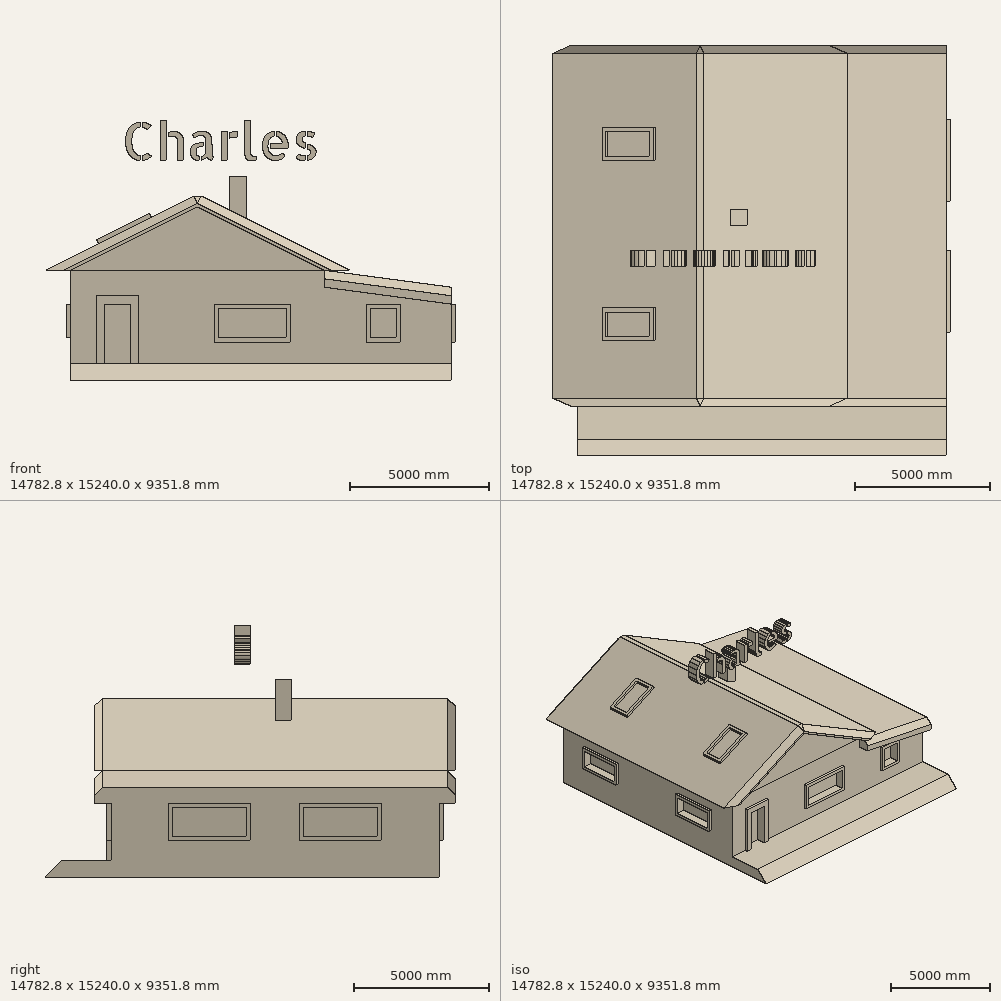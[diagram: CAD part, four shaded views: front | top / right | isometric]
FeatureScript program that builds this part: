
annotation { "Feature Type Name" : "Feature", "Feature Type Description" : "" }
export const myFeature = defineFeature(function(context is Context, id is Id, definition is map)
    precondition{}
    {
        {
            var Q0;
            Q0=qCreatedBy(makeId("Front.planeOp"),FACE);
            var sketch = newSketch(context, id + "F0", { "sketchPlane" : qUnion([Q0])});
            skLineSegment(sketch, "E0", {"start": v(0, 0) * mm, "end": v(4572, 0) * mm});
            skLineSegment(sketch, "E1", {"start": v(0, 0) * mm, "end": v(-4572, 0) * mm});
            skLineSegment(sketch, "E2", {"start": v(0, 0) * mm, "end": v(0, 2286) * mm});
            skLineSegment(sketch, "E3", {"start": v(0, 2286) * mm, "end": v(0, 2743.2) * mm});
            skLineSegment(sketch, "E4", {"start": v(-4572, 0) * mm, "end": v(-5486.4, 0) * mm});
            skLineSegment(sketch, "E5", {"start": v(4572, 0) * mm, "end": v(5486.4, 0) * mm});
            skLineSegment(sketch, "E6", {"start": v(0, 2286) * mm, "end": v(4572, 0) * mm});
            skLineSegment(sketch, "E7", {"start": v(0, 2286) * mm, "end": v(-4572, 0) * mm});
            skLineSegment(sketch, "E8", {"start": v(0, 2743.2) * mm, "end": v(-5486.4, 0) * mm});
            skLineSegment(sketch, "E9", {"start": v(0, 2743.2) * mm, "end": v(5486.4, 0) * mm});
            skLineSegment(sketch, "E10", {"start": v(-4572, 0) * mm, "end": v(-4572, -3352.8) * mm});
            skLineSegment(sketch, "E11", {"start": v(-4572, -3352.8) * mm, "end": v(4572, -3352.8) * mm});
            skLineSegment(sketch, "E12", {"start": v(4572, 0) * mm, "end": v(4572, -609.6) * mm});
            skLineSegment(sketch, "E13", {"start": v(4572, -609.6) * mm, "end": v(4572, -3352.8) * mm});
            skLineSegment(sketch, "E14", {"start": v(-4572, -3352.8) * mm, "end": v(-4572, -3962.4) * mm});
            skLineSegment(sketch, "E15", {"start": v(-4572, -3962.4) * mm, "end": v(4572, -3962.4) * mm});
            skLineSegment(sketch, "E16", {"start": v(4572, -3352.8) * mm, "end": v(4572, -3962.4) * mm});
            skLineSegment(sketch, "E17", {"start": v(4572, -3962.4) * mm, "end": v(9144, -3962.4) * mm});
            skLineSegment(sketch, "E18", {"start": v(4572, -3352.8) * mm, "end": v(9144, -3352.8) * mm});
            skLineSegment(sketch, "E19", {"start": v(9144, -3352.8) * mm, "end": v(9144, -3962.4) * mm});
            skLineSegment(sketch, "E20", {"start": v(9144, -3352.8) * mm, "end": v(9144, -609.6) * mm});
            skLineSegment(sketch, "E21", {"start": v(4572, 0) * mm, "end": v(9144, -609.6) * mm});
            skLineSegment(sketch, "E22", {"start": v(9144, -609.6) * mm, "end": v(9144, -1219.2) * mm});
            skLineSegment(sketch, "E23", {"start": v(4572, -609.6) * mm, "end": v(9144, -1219.2) * mm});
            skLineSegment(sketch, "E24", {"start": v(-3352.8, -3352.8) * mm, "end": v(-3352.8, -1219.2) * mm});
            skLineSegment(sketch, "E25", {"start": v(-2438.4, -3352.8) * mm, "end": v(-2438.4, -1219.2) * mm});
            skLineSegment(sketch, "E26", {"start": v(-2438.4, -1219.2) * mm, "end": v(-3352.8, -1219.2) * mm});
            skLineSegment(sketch, "E27", {"start": v(-3657.6, -3352.8) * mm, "end": v(-3657.6, -914.4) * mm});
            skLineSegment(sketch, "E28", {"start": v(-3657.6, -914.4) * mm, "end": v(-2133.6, -914.4) * mm});
            skLineSegment(sketch, "E29", {"start": v(-2133.6, -914.4) * mm, "end": v(-2133.6, -3352.8) * mm});
            skLineSegment(sketch, "E30.bottom", {"start": v(609.6, -1219.2) * mm, "end": v(3352.8, -1219.2) * mm});
            skLineSegment(sketch, "E30.top", {"start": v(609.6, -2590.8) * mm, "end": v(3352.8, -2590.8) * mm});
            skLineSegment(sketch, "E30.left", {"start": v(609.6, -1219.2) * mm, "end": v(609.6, -2590.8) * mm});
            skLineSegment(sketch, "E30.right", {"start": v(3352.8, -1219.2) * mm, "end": v(3352.8, -2590.8) * mm});
            skLineSegment(sketch, "E31.bottom", {"start": v(762, -1371.6) * mm, "end": v(3200.4, -1371.6) * mm});
            skLineSegment(sketch, "E31.top", {"start": v(762, -2438.4) * mm, "end": v(3200.4, -2438.4) * mm});
            skLineSegment(sketch, "E31.left", {"start": v(762, -1371.6) * mm, "end": v(762, -2438.4) * mm});
            skLineSegment(sketch, "E31.right", {"start": v(3200.4, -1371.6) * mm, "end": v(3200.4, -2438.4) * mm});
            skLineSegment(sketch, "E32.bottom", {"start": v(6096, -1219.2) * mm, "end": v(7315.2, -1219.2) * mm});
            skLineSegment(sketch, "E32.top", {"start": v(6096, -2590.8) * mm, "end": v(7315.2, -2590.8) * mm});
            skLineSegment(sketch, "E32.left", {"start": v(6096, -1219.2) * mm, "end": v(6096, -2590.8) * mm});
            skLineSegment(sketch, "E32.right", {"start": v(7315.2, -1219.2) * mm, "end": v(7315.2, -2590.8) * mm});
            skLineSegment(sketch, "E33.bottom", {"start": v(6248.4, -1371.6) * mm, "end": v(7162.8, -1371.6) * mm});
            skLineSegment(sketch, "E33.top", {"start": v(6248.4, -2438.4) * mm, "end": v(7162.8, -2438.4) * mm});
            skLineSegment(sketch, "E33.left", {"start": v(6248.4, -1371.6) * mm, "end": v(6248.4, -2438.4) * mm});
            skLineSegment(sketch, "E33.right", {"start": v(7162.8, -1371.6) * mm, "end": v(7162.8, -2438.4) * mm});
            skLineSegment(sketch, "E34", {"start": v(1746.97, 1869.71) * mm, "end": v(1746.97, 3393.71) * mm});
            skLineSegment(sketch, "E35", {"start": v(1746.97, 3393.71) * mm, "end": v(1137.37, 3393.71) * mm});
            skLineSegment(sketch, "E36", {"start": v(1137.37, 3393.71) * mm, "end": v(1137.37, 2174.51) * mm});
            skText(sketch, "E37", { "text": "Charles", "fontName": "AllertaStencil-Regular.ttf"});
            skLineSegment(sketch, "E38", {"start": v(-5486.4, 0) * mm, "end": v(-5486.4, 6096) * mm, "construction": true});
            const initialGuessF0  = {"E37": [-2.7432, 3.9624, 1, 0, 1.35413]};
            skSetInitialGuess(sketch, initialGuessF0);
            skSolve(sketch);
        }
        {
            var Q0;
            Q0=makeQuery(id+"F0.imprint","IMPRINT",FACE,{"disambiguationData":[TD([[makeQuery(id+"F0.imprint","IMPRINT",EDGE,{"derivedFrom":sQuery(id+"F0.wireOp",EDGE,"E3")}),1.0]])]});
            var Q1;
            Q1=makeQuery(id+"F0.imprint","IMPRINT",FACE,{"disambiguationData":[TD([[makeQuery(id+"F0.imprint","IMPRINT",EDGE,{"derivedFrom":sQuery(id+"F0.wireOp",EDGE,"E3")}),-1.0]])]});
            var Q2;
            Q2=makeQuery(id+"F0.imprint","IMPRINT",FACE,{"disambiguationData":[TD([[makeQuery(id+"F0.imprint","IMPRINT",EDGE,{"derivedFrom":sQuery(id+"F0.wireOp",EDGE,"E12")}),1.0]])]});
            extrude(context, id + "F1", {"entities" : qUnion([Q0, Q1, Q2]), "depth" : 12801.6 * mm, "offsetDistance" : 30.48 * mm, "hasSecondDirection" : true, "secondDirectionOppositeDirection" : true, "secondDirectionDepth" : 609.6 * mm});
        }
        {
            var Q0;
            Q0=makeQuery(id+"F0.imprint","IMPRINT",FACE,{"disambiguationData":[TD([[makeQuery(id+"F0.imprint","IMPRINT",EDGE,{"derivedFrom":sQuery(id+"F0.wireOp",EDGE,"E0")}),-1.0]])]});
            var Q1;
            Q1=makeQuery(id+"F0.imprint","IMPRINT",FACE,{"disambiguationData":[TD([[makeQuery(id+"F0.imprint","IMPRINT",EDGE,{"derivedFrom":sQuery(id+"F0.wireOp",EDGE,"E13")}),1.0]])]});
            extrude(context, id + "F2", {"entities" : qUnion([Q0, Q1]), "operationType" : NewBodyOperationType.ADD, "depth" : 12192 * mm, "offsetDistance" : 30.48 * mm});
        }
        {
            var Q0;
            Q0=makeQuery(id+"F0.imprint","IMPRINT",FACE,{"disambiguationData":[TD([[makeQuery(id+"F0.imprint","IMPRINT",EDGE,{"derivedFrom":sQuery(id+"F0.wireOp",EDGE,"E0")}),1.0]])]});
            var Q1;
            Q1=makeQuery(id+"F0.imprint","IMPRINT",FACE,{"disambiguationData":[TD([[makeQuery(id+"F0.imprint","IMPRINT",EDGE,{"derivedFrom":sQuery(id+"F0.wireOp",EDGE,"E1")}),-1.0]])]});
            extrude(context, id + "F3", {"entities" : qUnion([Q0, Q1]), "depth" : 12344.4 * mm, "offsetDistance" : 30.48 * mm, "hasSecondDirection" : true, "secondDirectionOppositeDirection" : true, "secondDirectionDepth" : 152.4 * mm});
        }
        {
            var Q0;
            {var subQ0=sQuery(id+"F0.wireOp",EDGE,"E24");Q0=makeQuery(id+"F0.imprint","IMPRINT",FACE,{"disambiguationData":[TD([[makeQuery(id+"F0.imprint","IMPRINT",EDGE,{"derivedFrom":subQ0}),1.0]])]});}
            var Q1;
            Q1=makeQuery(id+"F0.imprint","IMPRINT",FACE,{"disambiguationData":[TD([[makeQuery(id+"F0.imprint","IMPRINT",EDGE,{"derivedFrom":sQuery(id+"F0.wireOp",EDGE,"E30.bottom")}),-1.0]])]});
            var Q2;
            Q2=makeQuery(id+"F0.imprint","IMPRINT",FACE,{"disambiguationData":[TD([[makeQuery(id+"F0.imprint","IMPRINT",EDGE,{"derivedFrom":sQuery(id+"F0.wireOp",EDGE,"E32.bottom")}),-1.0]])]});
            extrude(context, id + "F4", {"entities" : qUnion([Q0, Q1, Q2]), "operationType" : NewBodyOperationType.ADD, "depth" : 12344.4 * mm, "offsetDistance" : 30.48 * mm});
        }
        {
            var Q0;
            Q0=makeQuery(id+"F0.imprint","IMPRINT",FACE,{"disambiguationData":[TD([[makeQuery(id+"F0.imprint","IMPRINT",EDGE,{"derivedFrom":sQuery(id+"F0.wireOp",EDGE,"E31.bottom")}),-1.0]])]});
            var Q1;
            Q1=makeQuery(id+"F0.imprint","IMPRINT",FACE,{"disambiguationData":[TD([[makeQuery(id+"F0.imprint","IMPRINT",EDGE,{"derivedFrom":sQuery(id+"F0.wireOp",EDGE,"E33.bottom")}),-1.0]])]});
            var Q2;
            {var subQ0=sQuery(id+"F0.wireOp",EDGE,"E24");Q2=makeQuery(id+"F0.imprint","IMPRINT",FACE,{"disambiguationData":[TD([[makeQuery(id+"F0.imprint","IMPRINT",EDGE,{"derivedFrom":subQ0}),-1.0]])]});}
            extrude(context, id + "F5", {"entities" : qUnion([Q0, Q1, Q2]), "operationType" : NewBodyOperationType.ADD, "depth" : 11887.2 * mm, "offsetDistance" : 30.48 * mm});
        }
        {
            var Q0;
            {var subQ5=sQuery(id+"F0.wireOp",EDGE,"E14");Q0=makeQuery(id+"F0.imprint","IMPRINT",FACE,{"disambiguationData":[TD([[makeQuery(id+"F0.imprint","IMPRINT",EDGE,{"derivedFrom":subQ5}),1.0]])]});}
            var Q1;
            Q1=makeQuery(id+"F0.imprint","IMPRINT",FACE,{"disambiguationData":[TD([[makeQuery(id+"F0.imprint","IMPRINT",EDGE,{"derivedFrom":sQuery(id+"F0.wireOp",EDGE,"E16")}),1.0]])]});
            extrude(context, id + "F6", {"entities" : qUnion([Q0, Q1]), "operationType" : NewBodyOperationType.ADD, "depth" : 15240 * mm, "offsetDistance" : 30.48 * mm});
        }
        {
            var Q0;
            Q0=makeQuery(id+"F6.opExtrude","CAP_EDGE",EDGE,{"disambiguationData":[OSD([sQuery(id+"F0.wireOp",EDGE,"E11"),sQuery(id+"F0.wireOp",EDGE,"E18")])],"isStart":false});
            chamfer(context, id + "F7", {"entities" : qUnion([Q0]), "width" : 1219.2 * mm, "tangentPropagation" : true});
        }
        {
            var Q0;
            Q0=makeQuery(id+"F6.boolean.opBoolean","MERGE",FACE,{"derivedFrom":[makeQuery(id+"F2.boolean.opBoolean","MERGE",FACE,{"derivedFrom":[makeQuery(id+"F1.opExtrude","SWEPT_FACE",FACE,{"disambiguationData":[OSD([sQuery(id+"F0.wireOp",EDGE,"E22")])]}),makeQuery(id+"F2.opExtrude","SWEPT_FACE",FACE,{"disambiguationData":[OSD([sQuery(id+"F0.wireOp",EDGE,"E20")])]})]}),makeQuery(id+"F6.opExtrude","SWEPT_FACE",FACE,{"disambiguationData":[OSD([sQuery(id+"F0.wireOp",EDGE,"E19")])]})]});
            var sketch = newSketch(context, id + "F8", { "sketchPlane" : qUnion([Q0])});
            skLineSegment(sketch, "E39.bottom", {"start": v(-10058.4, -1219.2) * mm, "end": v(-7010.4, -1219.2) * mm});
            skLineSegment(sketch, "E39.top", {"start": v(-10058.4, -2590.8) * mm, "end": v(-7010.4, -2590.8) * mm});
            skLineSegment(sketch, "E39.left", {"start": v(-10058.4, -1219.2) * mm, "end": v(-10058.4, -2590.8) * mm});
            skLineSegment(sketch, "E39.right", {"start": v(-7010.4, -1219.2) * mm, "end": v(-7010.4, -2590.8) * mm});
            skLineSegment(sketch, "E40.bottom", {"start": v(-9906, -1371.6) * mm, "end": v(-7162.8, -1371.6) * mm});
            skLineSegment(sketch, "E40.top", {"start": v(-9906, -2438.4) * mm, "end": v(-7162.8, -2438.4) * mm});
            skLineSegment(sketch, "E40.left", {"start": v(-9906, -1371.6) * mm, "end": v(-9906, -2438.4) * mm});
            skLineSegment(sketch, "E40.right", {"start": v(-7162.8, -1371.6) * mm, "end": v(-7162.8, -2438.4) * mm});
            skLineSegment(sketch, "E41", {"start": v(-12192, -3352.8) * mm, "end": v(0, -3352.8) * mm, "construction": true});
            skLineSegment(sketch, "E42", {"start": v(-12192, -1219.2) * mm, "end": v(-12192, -3352.8) * mm, "construction": true});
            skLineSegment(sketch, "E43", {"start": v(0, -3352.8) * mm, "end": v(0, -1219.2) * mm, "construction": true});
            skLineSegment(sketch, "E44.bottom", {"start": v(-5181.6, -1219.2) * mm, "end": v(-2133.6, -1219.2) * mm});
            skLineSegment(sketch, "E44.top", {"start": v(-5181.6, -2590.8) * mm, "end": v(-2133.6, -2590.8) * mm});
            skLineSegment(sketch, "E44.left", {"start": v(-5181.6, -1219.2) * mm, "end": v(-5181.6, -2590.8) * mm});
            skLineSegment(sketch, "E44.right", {"start": v(-2133.6, -1219.2) * mm, "end": v(-2133.6, -2590.8) * mm});
            skLineSegment(sketch, "E45.bottom", {"start": v(-5029.2, -1371.6) * mm, "end": v(-2286, -1371.6) * mm});
            skLineSegment(sketch, "E45.top", {"start": v(-5029.2, -2438.4) * mm, "end": v(-2286, -2438.4) * mm});
            skLineSegment(sketch, "E45.left", {"start": v(-5029.2, -1371.6) * mm, "end": v(-5029.2, -2438.4) * mm});
            skLineSegment(sketch, "E45.right", {"start": v(-2286, -1371.6) * mm, "end": v(-2286, -2438.4) * mm});
            skSolve(sketch);
        }
        {
            var Q0;
            Q0=makeQuery(id+"F8.imprint","IMPRINT",FACE,{"disambiguationData":[TD([[makeQuery(id+"F8.imprint","IMPRINT",EDGE,{"derivedFrom":sQuery(id+"F8.wireOp",EDGE,"E39.bottom")}),-1.0]])]});
            var Q1;
            Q1=makeQuery(id+"F8.imprint","IMPRINT",FACE,{"disambiguationData":[TD([[makeQuery(id+"F8.imprint","IMPRINT",EDGE,{"derivedFrom":sQuery(id+"F8.wireOp",EDGE,"E44.bottom")}),-1.0]])]});
            extrude(context, id + "F9", {"entities" : qUnion([Q0, Q1]), "operationType" : NewBodyOperationType.ADD, "depth" : 152.4 * mm, "offsetDistance" : 30.48 * mm});
        }
        {
            var Q0;
            Q0=makeQuery(id+"F9.boolean.opBoolean","SPLIT",FACE,{"disambiguationData":[TD([makeQuery(id+"F9.opExtrude","SWEPT_FACE",FACE,{"disambiguationData":[OSD([sQuery(id+"F8.wireOp",EDGE,"E40.bottom")])]})])],"derivedFrom":makeQuery(id+"F6.boolean.opBoolean","MERGE",FACE,{"derivedFrom":[makeQuery(id+"F2.boolean.opBoolean","MERGE",FACE,{"derivedFrom":[makeQuery(id+"F1.opExtrude","SWEPT_FACE",FACE,{"disambiguationData":[OSD([sQuery(id+"F0.wireOp",EDGE,"E22")])]}),makeQuery(id+"F2.opExtrude","SWEPT_FACE",FACE,{"disambiguationData":[OSD([sQuery(id+"F0.wireOp",EDGE,"E20")])]})]}),makeQuery(id+"F6.opExtrude","SWEPT_FACE",FACE,{"disambiguationData":[OSD([sQuery(id+"F0.wireOp",EDGE,"E19")])]})]})});
            var Q1;
            Q1=makeQuery(id+"F9.boolean.opBoolean","SPLIT",FACE,{"disambiguationData":[TD([makeQuery(id+"F9.opExtrude","SWEPT_FACE",FACE,{"disambiguationData":[OSD([sQuery(id+"F8.wireOp",EDGE,"E45.bottom")])]})])],"derivedFrom":makeQuery(id+"F6.boolean.opBoolean","MERGE",FACE,{"derivedFrom":[makeQuery(id+"F2.boolean.opBoolean","MERGE",FACE,{"derivedFrom":[makeQuery(id+"F1.opExtrude","SWEPT_FACE",FACE,{"disambiguationData":[OSD([sQuery(id+"F0.wireOp",EDGE,"E22")])]}),makeQuery(id+"F2.opExtrude","SWEPT_FACE",FACE,{"disambiguationData":[OSD([sQuery(id+"F0.wireOp",EDGE,"E20")])]})]}),makeQuery(id+"F6.opExtrude","SWEPT_FACE",FACE,{"disambiguationData":[OSD([sQuery(id+"F0.wireOp",EDGE,"E19")])]})]})});
            extrude(context, id + "F10", {"entities" : qUnion([Q0, Q1]), "operationType" : NewBodyOperationType.REMOVE, "oppositeDirection" : true, "depth" : 304.8 * mm, "offsetDistance" : 30.48 * mm});
        }
        {
            var Q0;
            Q0=makeQuery(id+"F0.imprint","IMPRINT",FACE,{"disambiguationData":[TD([[makeQuery(id+"F0.imprint","IMPRINT",EDGE,{"derivedFrom":sQuery(id+"F0.wireOp",EDGE,"E0")}),-1.0]])]});
            var sketch = newSketch(context, id + "F11", { "sketchPlane" : qUnion([Q0])});
            skLineSegment(sketch, "E46", {"start": v(9121.3, -3359.73) * mm, "end": v(-4572.38, -3359.73) * mm, "construction": true});
            skSolve(sketch);
        }
        {
            var Q0;
            {var subQ0=sQuery(id+"F0.wireOp",EDGE,"E18");var subQ1=sQuery(id+"F0.wireOp",EDGE,"E11");var subQ2=sQuery(id+"F0.wireOp",EDGE,"E33.right");var subQ3=sQuery(id+"F0.wireOp",EDGE,"E33.left");var subQ4=sQuery(id+"F0.wireOp",EDGE,"E33.top");var subQ5=sQuery(id+"F0.wireOp",EDGE,"E33.bottom");var subQ6=sQuery(id+"F0.wireOp",EDGE,"E31.right");var subQ7=sQuery(id+"F0.wireOp",EDGE,"E31.left");var subQ8=sQuery(id+"F0.wireOp",EDGE,"E31.top");var subQ9=sQuery(id+"F0.wireOp",EDGE,"E31.bottom");var subQ10=sQuery(id+"F0.wireOp",EDGE,"E26");var subQ11=sQuery(id+"F0.wireOp",EDGE,"E25");var subQ12=sQuery(id+"F0.wireOp",EDGE,"E24");var subQ13=sQuery(id+"F0.wireOp",EDGE,"E32.right");var subQ14=sQuery(id+"F0.wireOp",EDGE,"E32.left");var subQ15=sQuery(id+"F0.wireOp",EDGE,"E32.top");var subQ16=sQuery(id+"F0.wireOp",EDGE,"E32.bottom");var subQ17=sQuery(id+"F0.wireOp",EDGE,"E30.right");var subQ18=sQuery(id+"F0.wireOp",EDGE,"E30.left");var subQ19=sQuery(id+"F0.wireOp",EDGE,"E30.top");var subQ20=sQuery(id+"F0.wireOp",EDGE,"E30.bottom");var subQ21=sQuery(id+"F0.wireOp",EDGE,"E29");var subQ22=sQuery(id+"F0.wireOp",EDGE,"E28");var subQ23=sQuery(id+"F0.wireOp",EDGE,"E27");Q0=makeQuery(id+"F6.boolean.opBoolean","MERGE",FACE,{"derivedFrom":[makeQuery(id+"F5.boolean.opBoolean","MERGE",FACE,{"derivedFrom":[makeQuery(id+"F4.boolean.opBoolean","MERGE",FACE,{"derivedFrom":[makeQuery(id+"F2.opExtrude","CAP_FACE",FACE,{"disambiguationData":[OSD([sQuery(id+"F0.wireOp",EDGE,"E0"),sQuery(id+"F0.wireOp",EDGE,"E1"),sQuery(id+"F0.wireOp",EDGE,"E10"),subQ1,sQuery(id+"F0.wireOp",EDGE,"E12"),subQ0,sQuery(id+"F0.wireOp",EDGE,"E20"),sQuery(id+"F0.wireOp",EDGE,"E23"),subQ23,subQ22,subQ21,subQ20,subQ19,subQ18,subQ17,subQ16,subQ15,subQ14,subQ13])],"isStart":true}),makeQuery(id+"F4.opExtrude","CAP_FACE",FACE,{"disambiguationData":[OSD([subQ1,subQ12,subQ11,subQ10,subQ23,subQ22,subQ21])],"isStart":true}),makeQuery(id+"F4.opExtrude","CAP_FACE",FACE,{"disambiguationData":[OSD([subQ20,subQ19,subQ18,subQ17,subQ9,subQ8,subQ7,subQ6])],"isStart":true}),makeQuery(id+"F4.opExtrude","CAP_FACE",FACE,{"disambiguationData":[OSD([subQ16,subQ15,subQ14,subQ13,subQ5,subQ4,subQ3,subQ2])],"isStart":true})]}),makeQuery(id+"F5.opExtrude","CAP_FACE",FACE,{"disambiguationData":[OSD([subQ1,subQ12,subQ11,subQ10])],"isStart":true}),makeQuery(id+"F5.opExtrude","CAP_FACE",FACE,{"disambiguationData":[OSD([subQ9,subQ8,subQ7,subQ6])],"isStart":true}),makeQuery(id+"F5.opExtrude","CAP_FACE",FACE,{"disambiguationData":[OSD([subQ5,subQ4,subQ3,subQ2])],"isStart":true})]}),makeQuery(id+"F6.opExtrude","CAP_FACE",FACE,{"disambiguationData":[OSD([subQ1,sQuery(id+"F0.wireOp",EDGE,"E14"),sQuery(id+"F0.wireOp",EDGE,"E15"),sQuery(id+"F0.wireOp",EDGE,"E17"),subQ0,sQuery(id+"F0.wireOp",EDGE,"E19")])],"isStart":true})]});}
            var sketch = newSketch(context, id + "F12", { "sketchPlane" : qUnion([Q0])});
            skLineSegment(sketch, "E47.bottom", {"start": v(-3962.4, -1073.73) * mm, "end": v(2743.2, -1073.73) * mm});
            skLineSegment(sketch, "E47.top", {"start": v(-3962.4, -2597.73) * mm, "end": v(2743.2, -2597.73) * mm});
            skLineSegment(sketch, "E47.left", {"start": v(-3962.4, -1073.73) * mm, "end": v(-3962.4, -2597.73) * mm});
            skLineSegment(sketch, "E47.right", {"start": v(2743.2, -1073.73) * mm, "end": v(2743.2, -2597.73) * mm});
            skLineSegment(sketch, "E48.bottom", {"start": v(-3810, -1226.13) * mm, "end": v(2590.8, -1226.13) * mm});
            skLineSegment(sketch, "E48.top", {"start": v(-3810, -2445.33) * mm, "end": v(2590.8, -2445.33) * mm});
            skLineSegment(sketch, "E48.left", {"start": v(-3810, -1226.13) * mm, "end": v(-3810, -2445.33) * mm});
            skLineSegment(sketch, "E48.right", {"start": v(2590.8, -1226.13) * mm, "end": v(2590.8, -2445.33) * mm});
            skLineSegment(sketch, "E49", {"start": v(4572, 0) * mm, "end": v(4572, -3344) * mm, "construction": true});
            skSolve(sketch);
        }
        {
            var Q0;
            Q0 = qSketchRegion(id + "F12", true);
            extrude(context, id + "F13", {"entities" : qUnion([Q0]), "operationType" : NewBodyOperationType.ADD, "depth" : 152.4 * mm, "offsetDistance" : 30.48 * mm});
        }
        {
            var Q0;
            Q0=makeQuery(id+"F12.imprint","IMPRINT",FACE,{"disambiguationData":[TD([[makeQuery(id+"F12.imprint","IMPRINT",EDGE,{"derivedFrom":sQuery(id+"F12.wireOp",EDGE,"E48.bottom")}),-1.0]])]});
            extrude(context, id + "F14", {"entities" : qUnion([Q0]), "operationType" : NewBodyOperationType.REMOVE, "oppositeDirection" : true, "depth" : 304.8 * mm, "offsetDistance" : 30.48 * mm});
        }
        {
            var Q0;
            Q0=makeQuery(id+"F1.opExtrude","SWEPT_FACE",FACE,{"disambiguationData":[OSD([sQuery(id+"F0.wireOp",EDGE,"E8")])]});
            var sketch = newSketch(context, id + "F15", { "sketchPlane" : qUnion([Q0])});
            skLineSegment(sketch, "E50", {"start": v(-4907.19, 609.6) * mm, "end": v(-4907.19, -12801.6) * mm, "construction": true});
            skLineSegment(sketch, "E51", {"start": v(-4907.19, -12801.6) * mm, "end": v(-335.19, -12801.6) * mm, "construction": true});
            skLineSegment(sketch, "E52", {"start": v(-4907.19, 609.6) * mm, "end": v(-335.19, 609.6) * mm, "construction": true});
            skLineSegment(sketch, "E53.bottom", {"start": v(-639.99, -2438.4) * mm, "end": v(-2773.59, -2438.4) * mm});
            skLineSegment(sketch, "E53.top", {"start": v(-639.99, -3657.6) * mm, "end": v(-2773.59, -3657.6) * mm});
            skLineSegment(sketch, "E53.left", {"start": v(-639.99, -2438.4) * mm, "end": v(-639.99, -3657.6) * mm});
            skLineSegment(sketch, "E53.right", {"start": v(-2773.59, -2438.4) * mm, "end": v(-2773.59, -3657.6) * mm});
            skLineSegment(sketch, "E54.bottom", {"start": v(-792.39, -2590.8) * mm, "end": v(-2621.19, -2590.8) * mm});
            skLineSegment(sketch, "E54.top", {"start": v(-792.39, -3505.2) * mm, "end": v(-2621.19, -3505.2) * mm});
            skLineSegment(sketch, "E54.left", {"start": v(-792.39, -2590.8) * mm, "end": v(-792.39, -3505.2) * mm});
            skLineSegment(sketch, "E54.right", {"start": v(-2621.19, -2590.8) * mm, "end": v(-2621.19, -3505.2) * mm});
            skLineSegment(sketch, "E55.bottom", {"start": v(-639.99, -9144) * mm, "end": v(-2773.59, -9144) * mm});
            skLineSegment(sketch, "E55.top", {"start": v(-639.99, -10363.2) * mm, "end": v(-2773.59, -10363.2) * mm});
            skLineSegment(sketch, "E55.left", {"start": v(-639.99, -9144) * mm, "end": v(-639.99, -10363.2) * mm});
            skLineSegment(sketch, "E55.right", {"start": v(-2773.59, -9144) * mm, "end": v(-2773.59, -10363.2) * mm});
            skLineSegment(sketch, "E56.bottom", {"start": v(-792.39, -9296.4) * mm, "end": v(-2621.19, -9296.4) * mm});
            skLineSegment(sketch, "E56.top", {"start": v(-792.39, -10210.8) * mm, "end": v(-2621.19, -10210.8) * mm});
            skLineSegment(sketch, "E56.left", {"start": v(-792.39, -9296.4) * mm, "end": v(-792.39, -10210.8) * mm});
            skLineSegment(sketch, "E56.right", {"start": v(-2621.19, -9296.4) * mm, "end": v(-2621.19, -10210.8) * mm});
            skSolve(sketch);
        }
        {
            var Q0;
            Q0=makeQuery(id+"F15.imprint","IMPRINT",FACE,{"disambiguationData":[TD([[makeQuery(id+"F15.imprint","IMPRINT",EDGE,{"derivedFrom":sQuery(id+"F15.wireOp",EDGE,"E53.bottom")}),1.0]])]});
            var Q1;
            Q1=makeQuery(id+"F15.imprint","IMPRINT",FACE,{"disambiguationData":[TD([[makeQuery(id+"F15.imprint","IMPRINT",EDGE,{"derivedFrom":sQuery(id+"F15.wireOp",EDGE,"E55.bottom")}),1.0]])]});
            extrude(context, id + "F16", {"entities" : qUnion([Q0, Q1]), "operationType" : NewBodyOperationType.ADD, "depth" : 152.4 * mm, "offsetDistance" : 30.48 * mm});
        }
        {
            var Q0;
            Q0=makeQuery(id+"F0.imprint","IMPRINT",FACE,{"disambiguationData":[TD([[makeQuery(id+"F0.imprint","IMPRINT",EDGE,{"derivedFrom":sQuery(id+"F0.wireOp",EDGE,"E37.sketch_text.stroke-107")}),-1.0]])]});
            var Q1;
            Q1=makeQuery(id+"F0.imprint","IMPRINT",FACE,{"disambiguationData":[TD([[makeQuery(id+"F0.imprint","IMPRINT",EDGE,{"derivedFrom":sQuery(id+"F0.wireOp",EDGE,"E37.sketch_text.stroke-114")}),-1.0]])]});
            var Q2;
            Q2=makeQuery(id+"F0.imprint","IMPRINT",FACE,{"disambiguationData":[TD([[makeQuery(id+"F0.imprint","IMPRINT",EDGE,{"derivedFrom":sQuery(id+"F0.wireOp",EDGE,"E37.sketch_text.stroke-121")}),-1.0]])]});
            var Q3;
            Q3=makeQuery(id+"F0.imprint","IMPRINT",FACE,{"disambiguationData":[TD([[makeQuery(id+"F0.imprint","IMPRINT",EDGE,{"derivedFrom":sQuery(id+"F0.wireOp",EDGE,"E37.sketch_text.stroke-152")}),-1.0]])]});
            var Q4;
            Q4=makeQuery(id+"F0.imprint","IMPRINT",FACE,{"disambiguationData":[TD([[makeQuery(id+"F0.imprint","IMPRINT",EDGE,{"derivedFrom":sQuery(id+"F0.wireOp",EDGE,"E37.sketch_text.stroke-139")}),-1.0]])]});
            var Q5;
            Q5=makeQuery(id+"F0.imprint","IMPRINT",FACE,{"disambiguationData":[TD([[makeQuery(id+"F0.imprint","IMPRINT",EDGE,{"derivedFrom":sQuery(id+"F0.wireOp",EDGE,"E37.sketch_text.stroke-176")}),-1.0]])]});
            var Q6;
            Q6=makeQuery(id+"F0.imprint","IMPRINT",FACE,{"disambiguationData":[TD([[makeQuery(id+"F0.imprint","IMPRINT",EDGE,{"derivedFrom":sQuery(id+"F0.wireOp",EDGE,"E37.sketch_text.stroke-190")}),-1.0]])]});
            var Q7;
            Q7=makeQuery(id+"F0.imprint","IMPRINT",FACE,{"disambiguationData":[TD([[makeQuery(id+"F0.imprint","IMPRINT",EDGE,{"derivedFrom":sQuery(id+"F0.wireOp",EDGE,"E37.sketch_text.stroke-205")}),-1.0]])]});
            var Q8;
            Q8=makeQuery(id+"F0.imprint","IMPRINT",FACE,{"disambiguationData":[TD([[makeQuery(id+"F0.imprint","IMPRINT",EDGE,{"derivedFrom":sQuery(id+"F0.wireOp",EDGE,"E37.sketch_text.stroke-196")}),-1.0]])]});
            var Q9;
            Q9=makeQuery(id+"F0.imprint","IMPRINT",FACE,{"disambiguationData":[TD([[makeQuery(id+"F0.imprint","IMPRINT",EDGE,{"derivedFrom":sQuery(id+"F0.wireOp",EDGE,"E37.sketch_text.stroke-71")}),-1.0]])]});
            var Q10;
            Q10=makeQuery(id+"F0.imprint","IMPRINT",FACE,{"disambiguationData":[TD([[makeQuery(id+"F0.imprint","IMPRINT",EDGE,{"derivedFrom":sQuery(id+"F0.wireOp",EDGE,"E37.sketch_text.stroke-52")}),-1.0]])]});
            var Q11;
            Q11=makeQuery(id+"F0.imprint","IMPRINT",FACE,{"disambiguationData":[TD([[makeQuery(id+"F0.imprint","IMPRINT",EDGE,{"derivedFrom":sQuery(id+"F0.wireOp",EDGE,"E37.sketch_text.stroke-29")}),-1.0]])]});
            var Q12;
            Q12=makeQuery(id+"F0.imprint","IMPRINT",FACE,{"disambiguationData":[TD([[makeQuery(id+"F0.imprint","IMPRINT",EDGE,{"derivedFrom":sQuery(id+"F0.wireOp",EDGE,"E37.sketch_text.stroke-33")}),-1.0]])]});
            var Q13;
            Q13=makeQuery(id+"F0.imprint","IMPRINT",FACE,{"disambiguationData":[TD([[makeQuery(id+"F0.imprint","IMPRINT",EDGE,{"derivedFrom":sQuery(id+"F0.wireOp",EDGE,"E37.sketch_text.stroke-11")}),-1.0]])]});
            var Q14;
            Q14=makeQuery(id+"F0.imprint","IMPRINT",FACE,{"disambiguationData":[TD([[makeQuery(id+"F0.imprint","IMPRINT",EDGE,{"derivedFrom":sQuery(id+"F0.wireOp",EDGE,"E37.sketch_text.stroke-0")}),-1.0]])]});
            var Q15;
            Q15=makeQuery(id+"F0.imprint","IMPRINT",FACE,{"disambiguationData":[TD([[makeQuery(id+"F0.imprint","IMPRINT",EDGE,{"derivedFrom":sQuery(id+"F0.wireOp",EDGE,"E37.sketch_text.stroke-5")}),-1.0]])]});
            extrude(context, id + "F17", {"entities" : qUnion([Q0, Q1, Q2, Q3, Q4, Q5, Q6, Q7, Q8, Q9, Q10, Q11, Q12, Q13, Q14, Q15]), "depth" : 7620 * mm, "offsetDistance" : 30.48 * mm, "hasSecondDirection" : true, "secondDirectionOppositeDirection" : false, "secondDirectionDepth" : 7010.4 * mm});
        }
        {
            var Q0;
            Q0=makeQuery(id+"F1.opExtrude","CAP_EDGE",EDGE,{"disambiguationData":[OSD([sQuery(id+"F0.wireOp",EDGE,"E9")])],"isStart":true});
            var Q1;
            Q1=makeQuery(id+"F1.opExtrude","CAP_EDGE",EDGE,{"disambiguationData":[OSD([sQuery(id+"F0.wireOp",EDGE,"E8")])],"isStart":true});
            var Q2;
            Q2=makeQuery(id+"F1.opExtrude","CAP_EDGE",EDGE,{"disambiguationData":[OSD([sQuery(id+"F0.wireOp",EDGE,"E8")])],"isStart":false});
            var Q3;
            Q3=makeQuery(id+"F1.opExtrude","CAP_EDGE",EDGE,{"disambiguationData":[OSD([sQuery(id+"F0.wireOp",EDGE,"E9")])],"isStart":false});
            var Q4;
            Q4=makeQuery(id+"F1.opExtrude","SWEPT_EDGE",EDGE,{"disambiguationData":[OSD([sQuery(id+"F0.wireOp",EDGE,"E3"),sQuery(id+"F0.wireOp",EDGE,"E8"),sQuery(id+"F0.wireOp",EDGE,"E9")])]});
            var Q5;
            Q5=makeQuery(id+"F1.opExtrude","CAP_EDGE",EDGE,{"disambiguationData":[OSD([sQuery(id+"F0.wireOp",EDGE,"E21")])],"isStart":true});
            var Q6;
            Q6=makeQuery(id+"F1.opExtrude","CAP_EDGE",EDGE,{"disambiguationData":[OSD([sQuery(id+"F0.wireOp",EDGE,"E21")])],"isStart":false});
            chamfer(context, id + "F18", {"entities" : qUnion([Q0, Q1, Q2, Q3, Q4, Q5, Q6]), "width" : 304.8 * mm, "tangentPropagation" : true});
        }
        {
            var Q0;
            Q0=makeQuery(id+"F6.boolean.opBoolean","MERGE",FACE,{"derivedFrom":[makeQuery(id+"F2.opExtrude","SWEPT_FACE",FACE,{"disambiguationData":[OSD([sQuery(id+"F0.wireOp",EDGE,"E10")])]}),makeQuery(id+"F6.opExtrude","SWEPT_FACE",FACE,{"disambiguationData":[OSD([sQuery(id+"F0.wireOp",EDGE,"E14")])]})]});
            var sketch = newSketch(context, id + "F19", { "sketchPlane" : qUnion([Q0])});
            skLineSegment(sketch, "E57", {"start": v(12192, -3352.8) * mm, "end": v(0, -3352.8) * mm, "construction": true});
            skLineSegment(sketch, "E58", {"start": v(12192, 0) * mm, "end": v(12192, -3352.8) * mm, "construction": true});
            skLineSegment(sketch, "E59", {"start": v(0, -3352.8) * mm, "end": v(0, 0) * mm, "construction": true});
            skLineSegment(sketch, "E60.bottom", {"start": v(1524, -1219.2) * mm, "end": v(3962.4, -1219.2) * mm});
            skLineSegment(sketch, "E60.top", {"start": v(1524, -2438.4) * mm, "end": v(3962.4, -2438.4) * mm});
            skLineSegment(sketch, "E60.left", {"start": v(1524, -1219.2) * mm, "end": v(1524, -2438.4) * mm});
            skLineSegment(sketch, "E60.right", {"start": v(3962.4, -1219.2) * mm, "end": v(3962.4, -2438.4) * mm});
            skLineSegment(sketch, "E61.bottom", {"start": v(1676.4, -1371.6) * mm, "end": v(3810, -1371.6) * mm});
            skLineSegment(sketch, "E61.top", {"start": v(1676.4, -2286) * mm, "end": v(3810, -2286) * mm});
            skLineSegment(sketch, "E61.left", {"start": v(1676.4, -1371.6) * mm, "end": v(1676.4, -2286) * mm});
            skLineSegment(sketch, "E61.right", {"start": v(3810, -1371.6) * mm, "end": v(3810, -2286) * mm});
            skLineSegment(sketch, "E62.bottom", {"start": v(8229.6, -1219.2) * mm, "end": v(10668, -1219.2) * mm});
            skLineSegment(sketch, "E62.top", {"start": v(8229.6, -2438.4) * mm, "end": v(10668, -2438.4) * mm});
            skLineSegment(sketch, "E62.left", {"start": v(8229.6, -1219.2) * mm, "end": v(8229.6, -2438.4) * mm});
            skLineSegment(sketch, "E62.right", {"start": v(10668, -1219.2) * mm, "end": v(10668, -2438.4) * mm});
            skLineSegment(sketch, "E63.bottom", {"start": v(8382, -1371.6) * mm, "end": v(10515.6, -1371.6) * mm});
            skLineSegment(sketch, "E63.top", {"start": v(8382, -2286) * mm, "end": v(10515.6, -2286) * mm});
            skLineSegment(sketch, "E63.left", {"start": v(8382, -1371.6) * mm, "end": v(8382, -2286) * mm});
            skLineSegment(sketch, "E63.right", {"start": v(10515.6, -1371.6) * mm, "end": v(10515.6, -2286) * mm});
            skSolve(sketch);
        }
        {
            var Q0;
            Q0=makeQuery(id+"F19.imprint","IMPRINT",FACE,{"disambiguationData":[TD([[makeQuery(id+"F19.imprint","IMPRINT",EDGE,{"derivedFrom":sQuery(id+"F19.wireOp",EDGE,"E60.bottom")}),-1.0]])]});
            var Q1;
            Q1=makeQuery(id+"F19.imprint","IMPRINT",FACE,{"disambiguationData":[TD([[makeQuery(id+"F19.imprint","IMPRINT",EDGE,{"derivedFrom":sQuery(id+"F19.wireOp",EDGE,"E62.bottom")}),-1.0]])]});
            extrude(context, id + "F20", {"entities" : qUnion([Q0, Q1]), "operationType" : NewBodyOperationType.ADD, "depth" : 152.4 * mm, "offsetDistance" : 30.48 * mm});
        }
        {
            var Q0;
            Q0=makeQuery(id+"F20.boolean.opBoolean","SPLIT",FACE,{"disambiguationData":[TD([makeQuery(id+"F20.opExtrude","SWEPT_FACE",FACE,{"disambiguationData":[OSD([sQuery(id+"F19.wireOp",EDGE,"E61.bottom")])]})])],"derivedFrom":makeQuery(id+"F6.boolean.opBoolean","MERGE",FACE,{"derivedFrom":[makeQuery(id+"F2.opExtrude","SWEPT_FACE",FACE,{"disambiguationData":[OSD([sQuery(id+"F0.wireOp",EDGE,"E10")])]}),makeQuery(id+"F6.opExtrude","SWEPT_FACE",FACE,{"disambiguationData":[OSD([sQuery(id+"F0.wireOp",EDGE,"E14")])]})]})});
            var Q1;
            Q1=makeQuery(id+"F20.boolean.opBoolean","SPLIT",FACE,{"disambiguationData":[TD([makeQuery(id+"F20.opExtrude","SWEPT_FACE",FACE,{"disambiguationData":[OSD([sQuery(id+"F19.wireOp",EDGE,"E63.bottom")])]})])],"derivedFrom":makeQuery(id+"F6.boolean.opBoolean","MERGE",FACE,{"derivedFrom":[makeQuery(id+"F2.opExtrude","SWEPT_FACE",FACE,{"disambiguationData":[OSD([sQuery(id+"F0.wireOp",EDGE,"E10")])]}),makeQuery(id+"F6.opExtrude","SWEPT_FACE",FACE,{"disambiguationData":[OSD([sQuery(id+"F0.wireOp",EDGE,"E14")])]})]})});
            extrude(context, id + "F21", {"entities" : qUnion([Q0, Q1]), "operationType" : NewBodyOperationType.REMOVE, "oppositeDirection" : true, "depth" : 304.8 * mm, "offsetDistance" : 30.48 * mm});
        }
        {
            var Q0;
            {var subQ0=sQuery(id+"F0.wireOp",EDGE,"E34");Q0=makeQuery(id+"F0.imprint","IMPRINT",FACE,{"disambiguationData":[TD([[makeQuery(id+"F0.imprint","IMPRINT",EDGE,{"derivedFrom":subQ0}),1.0]])]});}
            extrude(context, id + "F22", {"entities" : qUnion([Q0]), "operationType" : NewBodyOperationType.ADD, "depth" : 6096 * mm, "offsetDistance" : 30.48 * mm, "hasSecondDirection" : true, "secondDirectionOppositeDirection" : false, "secondDirectionDepth" : 5486.4 * mm});
        }
    });
